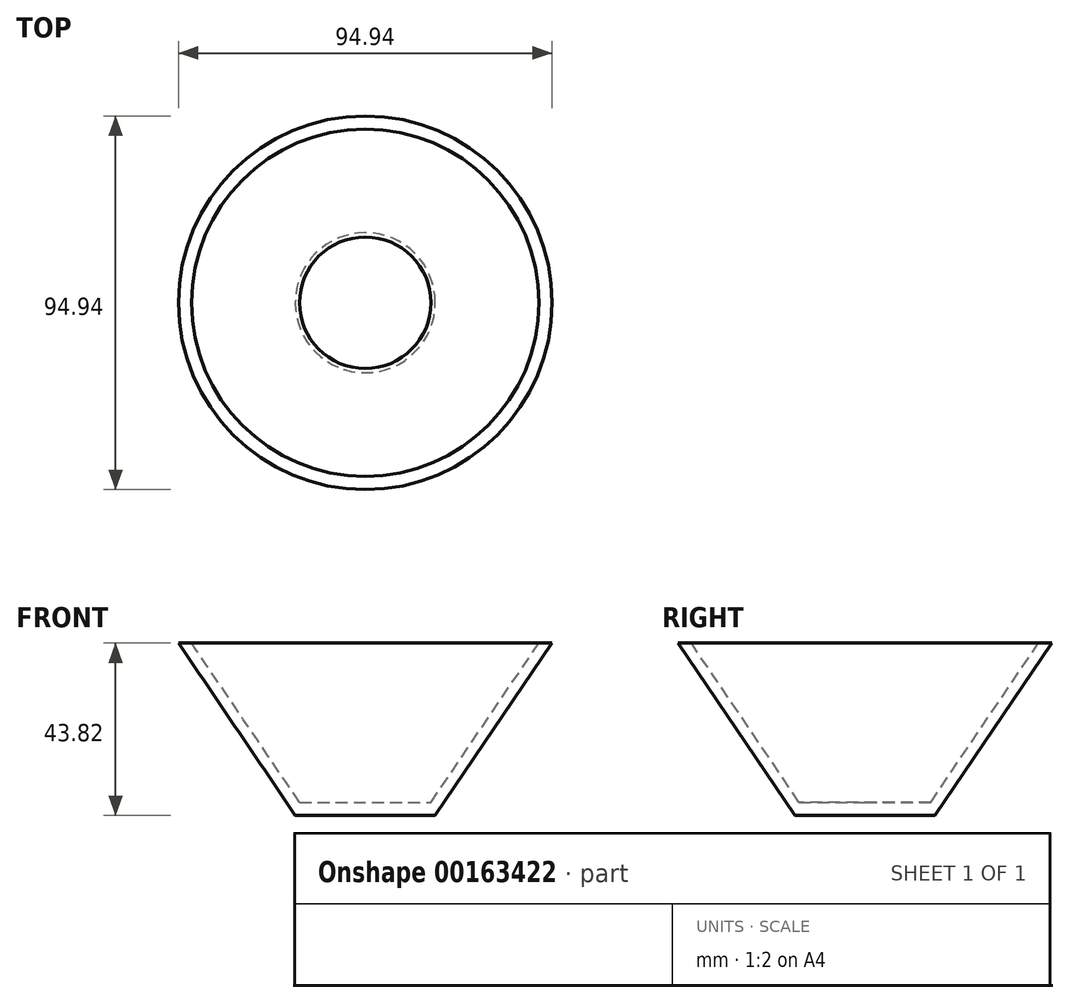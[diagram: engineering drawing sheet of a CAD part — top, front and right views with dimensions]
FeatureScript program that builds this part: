
annotation { "Feature Type Name" : "Feature", "Feature Type Description" : "" }
export const myFeature = defineFeature(function(context is Context, id is Id, definition is map)
    precondition{}
    {
        {
            var Q0;
            Q0=qCreatedBy(makeId("Front.planeOp"),FACE);
            var sketch = newSketch(context, id + "F0", { "sketchPlane" : qUnion([Q0])});
            skLineSegment(sketch, "E0", {"start": v(-47.47, 43.81) * mm, "end": v(-17.78, 0) * mm});
            skLineSegment(sketch, "E1", {"start": v(-17.78, 0) * mm, "end": v(0, 0) * mm});
            skLineSegment(sketch, "E2", {"start": v(0, 0) * mm, "end": v(0, 3.35) * mm});
            skLineSegment(sketch, "E3", {"start": v(0, 3.35) * mm, "end": v(-16.7, 3.35) * mm});
            skLineSegment(sketch, "E4", {"start": v(-16.7, 3.35) * mm, "end": v(-44.11, 43.82) * mm});
            skLineSegment(sketch, "E5", {"start": v(-44.11, 43.81) * mm, "end": v(-47.47, 43.81) * mm});
            skSolve(sketch);
        }
        {
            var Q0;
            Q0=makeQuery(id+"F0.imprint","IMPRINT",FACE,{"disambiguationData":[TD([[makeQuery(id+"F0.imprint","IMPRINT",EDGE,{"derivedFrom":sQuery(id+"F0.wireOp",EDGE,"E0")}),1.0]])]});
            var Q1;
            Q1=sQuery(id+"F0.wireOp",EDGE,"E2");
            revolve(context, id + "F1", {"entities" : qUnion([Q0]), "axis" : qUnion([Q1]), "revolveType" : RevolveType.FULL});
        }
    });
